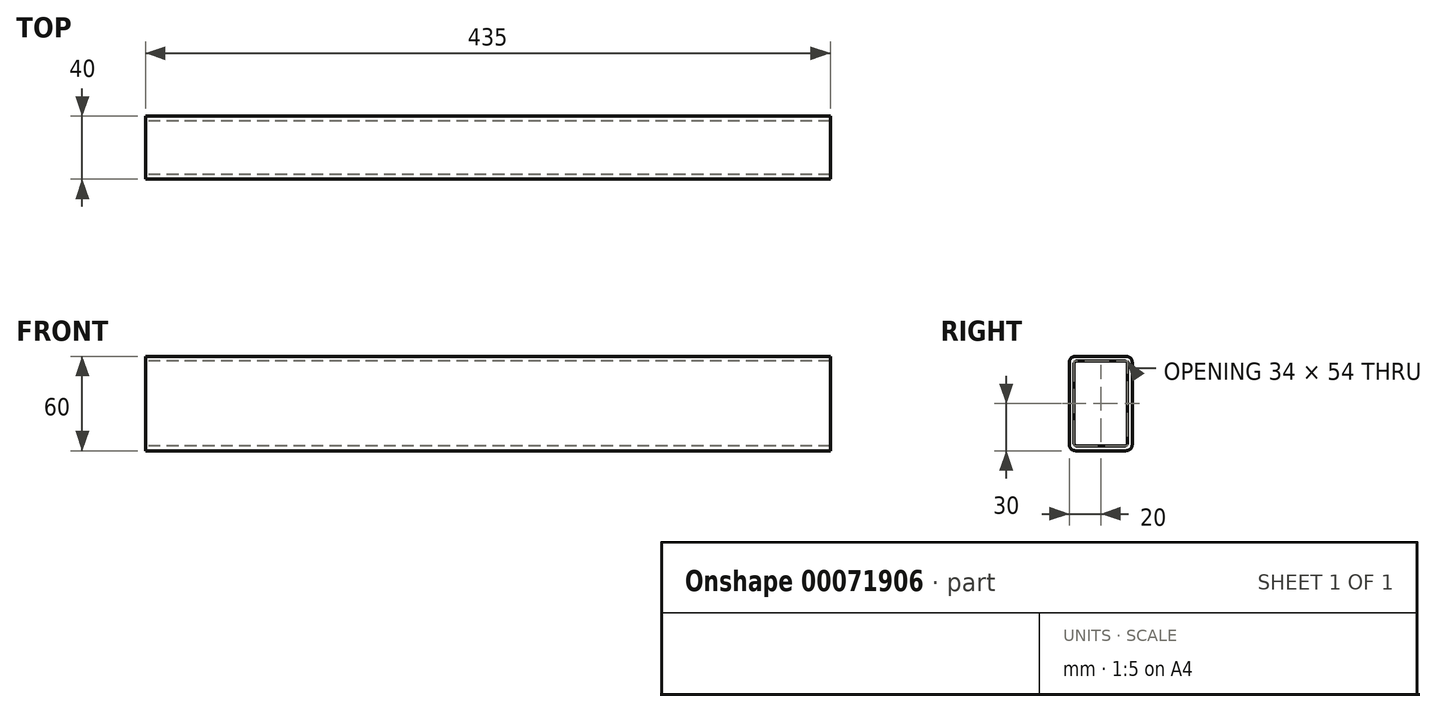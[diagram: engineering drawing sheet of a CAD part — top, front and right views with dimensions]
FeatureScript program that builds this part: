
annotation { "Feature Type Name" : "Feature", "Feature Type Description" : "" }
export const myFeature = defineFeature(function(context is Context, id is Id, definition is map)
    precondition{}
    {
        {
            var Q0;
            Q0=qCreatedBy(makeId("Right.planeOp"),FACE);
            var sketch = newSketch(context, id + "F0", { "sketchPlane" : qUnion([Q0])});
            skLineSegment(sketch, "E0.bottom", {"start": v(-16, 30) * mm, "end": v(16, 30) * mm});
            skLineSegment(sketch, "E0.top", {"start": v(-16, -30) * mm, "end": v(16, -30) * mm});
            skLineSegment(sketch, "E0.left", {"start": v(-20, 26) * mm, "end": v(-20, -26) * mm});
            skLineSegment(sketch, "E0.right", {"start": v(20, 26) * mm, "end": v(20, -26) * mm});
            skPoint(sketch, "E0.middle", {"position": v(0, 0) * mm});
            skLineSegment(sketch, "E1.bottom", {"start": v(-15, 27) * mm, "end": v(15, 27) * mm});
            skLineSegment(sketch, "E1.top", {"start": v(-15, -27) * mm, "end": v(15, -27) * mm});
            skLineSegment(sketch, "E1.left", {"start": v(-17, 25) * mm, "end": v(-17, -25) * mm});
            skLineSegment(sketch, "E1.right", {"start": v(17, 25) * mm, "end": v(17, -25) * mm});
            skPoint(sketch, "E2.visualSharp", {"position": v(-20, 30) * mm});
            skArc(sketch, "E2.filletArc", {"start": v(-16, 30) * mm, "mid": v(-18.83, 28.83) * mm, "end": v(-20, 26) * mm});
            skPoint(sketch, "E3.visualSharp", {"position": v(-20, -30) * mm});
            skArc(sketch, "E3.filletArc", {"start": v(-20, -26) * mm, "mid": v(-18.83, -28.83) * mm, "end": v(-16, -30) * mm});
            skPoint(sketch, "E4.visualSharp", {"position": v(20, -30) * mm});
            skArc(sketch, "E4.filletArc", {"start": v(16, -30) * mm, "mid": v(18.83, -28.83) * mm, "end": v(20, -26) * mm});
            skPoint(sketch, "E5.visualSharp", {"position": v(20, 30) * mm});
            skArc(sketch, "E5.filletArc", {"start": v(20, 26) * mm, "mid": v(18.83, 28.83) * mm, "end": v(16, 30) * mm});
            skPoint(sketch, "E6.visualSharp", {"position": v(17, 27) * mm});
            skArc(sketch, "E6.filletArc", {"start": v(17, 25) * mm, "mid": v(16.41, 26.41) * mm, "end": v(15, 27) * mm});
            skPoint(sketch, "E7.visualSharp", {"position": v(17, -27) * mm});
            skArc(sketch, "E7.filletArc", {"start": v(15, -27) * mm, "mid": v(16.41, -26.41) * mm, "end": v(17, -25) * mm});
            skPoint(sketch, "E8.visualSharp", {"position": v(-17, -27) * mm});
            skArc(sketch, "E8.filletArc", {"start": v(-17, -25) * mm, "mid": v(-16.41, -26.41) * mm, "end": v(-15, -27) * mm});
            skPoint(sketch, "E9.visualSharp", {"position": v(-17, 27) * mm});
            skArc(sketch, "E9.filletArc", {"start": v(-15, 27) * mm, "mid": v(-16.41, 26.41) * mm, "end": v(-17, 25) * mm});
            skSolve(sketch);
        }
        {
            var Q0;
            Q0=makeQuery(id+"F0.imprint","IMPRINT",FACE,{"disambiguationData":[TD([[makeQuery(id+"F0.imprint","IMPRINT",EDGE,{"derivedFrom":sQuery(id+"F0.wireOp",EDGE,"E0.bottom")}),-1.0]])]});
            extrude(context, id + "F1", {"entities" : qUnion([Q0]), "depth" : 435 * mm});
        }
    });
